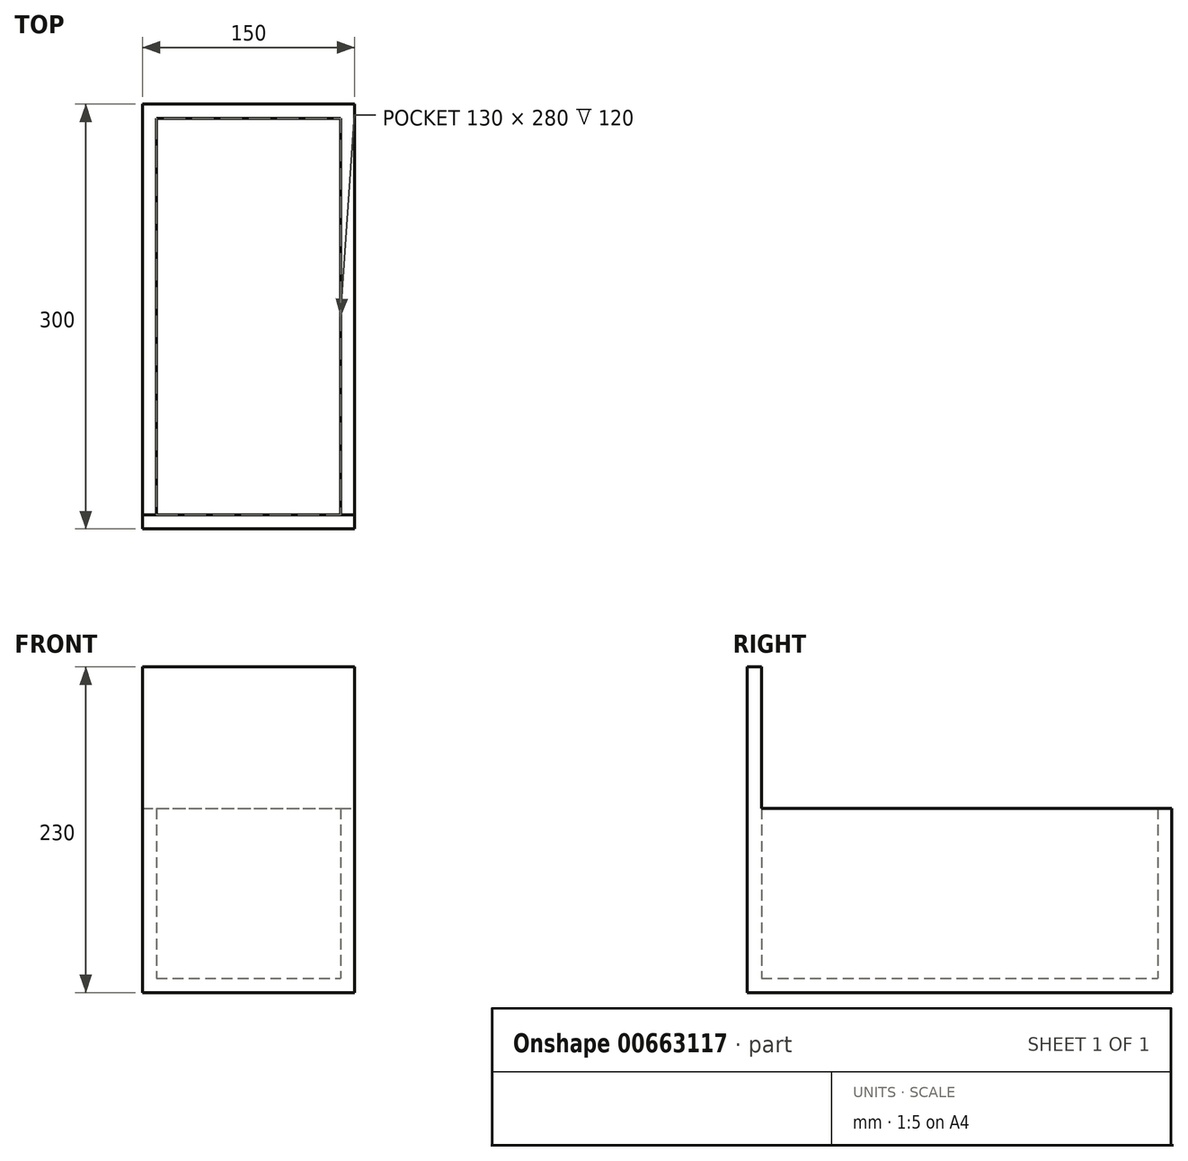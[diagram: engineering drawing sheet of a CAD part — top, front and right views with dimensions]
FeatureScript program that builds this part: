
annotation { "Feature Type Name" : "Feature", "Feature Type Description" : "" }
export const myFeature = defineFeature(function(context is Context, id is Id, definition is map)
    precondition{}
    {
        {
            var Q0;
            Q0=qCreatedBy(makeId("Top.planeOp"),FACE);
            var sketch = newSketch(context, id + "F0", { "sketchPlane" : qUnion([Q0])});
            skLineSegment(sketch, "E0.bottom", {"start": v(-75, -150) * mm, "end": v(75, -150) * mm});
            skLineSegment(sketch, "E0.top", {"start": v(-75, 150) * mm, "end": v(75, 150) * mm});
            skLineSegment(sketch, "E0.left", {"start": v(-75, -150) * mm, "end": v(-75, 150) * mm});
            skLineSegment(sketch, "E0.right", {"start": v(75, -150) * mm, "end": v(75, 150) * mm});
            skPoint(sketch, "E0.middle", {"position": v(0, 0) * mm});
            skSolve(sketch);
        }
        {
            var Q0;
            Q0=makeQuery(id+"F0.imprint","IMPRINT",FACE,{"disambiguationData":[TD([[makeQuery(id+"F0.imprint","IMPRINT",EDGE,{"derivedFrom":sQuery(id+"F0.wireOp",EDGE,"E0.bottom")}),1.0]])]});
            extrude(context, id + "F1", {"entities" : qUnion([Q0]), "depth" : 130 * mm, "offsetDistance" : 25 * mm});
        }
        {
            var Q0;
            Q0=makeQuery(id+"F1.opExtrude","CAP_FACE",FACE,{"disambiguationData":[OSD([sQuery(id+"F0.wireOp",EDGE,"E0.bottom"),sQuery(id+"F0.wireOp",EDGE,"E0.top"),sQuery(id+"F0.wireOp",EDGE,"E0.left"),sQuery(id+"F0.wireOp",EDGE,"E0.right")])],"isStart":false});
            shell(context, id + "F2", {"entities" : qUnion([Q0]), "thickness" : 10 * mm});
        }
        {
            var Q0;
            Q0=makeQuery(id+"F1.opExtrude","CAP_FACE",FACE,{"disambiguationData":[OSD([sQuery(id+"F0.wireOp",EDGE,"E0.bottom"),sQuery(id+"F0.wireOp",EDGE,"E0.top"),sQuery(id+"F0.wireOp",EDGE,"E0.left"),sQuery(id+"F0.wireOp",EDGE,"E0.right")])],"isStart":false});
            var sketch = newSketch(context, id + "F3", { "sketchPlane" : qUnion([Q0])});
            skLineSegment(sketch, "E1.bottom", {"start": v(-75, -150) * mm, "end": v(75, -150) * mm});
            skLineSegment(sketch, "E1.top", {"start": v(-75, -140) * mm, "end": v(75, -140) * mm});
            skLineSegment(sketch, "E1.left", {"start": v(-75, -150) * mm, "end": v(-75, -140) * mm});
            skLineSegment(sketch, "E1.right", {"start": v(75, -150) * mm, "end": v(75, -140) * mm});
            skSolve(sketch);
        }
        {
            var Q0;
            Q0=makeQuery(id+"F3.imprint","IMPRINT",FACE,{"disambiguationData":[TD([[makeQuery(id+"F3.imprint","IMPRINT",EDGE,{"derivedFrom":sQuery(id+"F3.wireOp",EDGE,"E1.bottom")}),1.0]])]});
            extrude(context, id + "F4", {"entities" : qUnion([Q0]), "operationType" : NewBodyOperationType.ADD, "depth" : 100 * mm, "offsetDistance" : 25 * mm});
        }
    });
